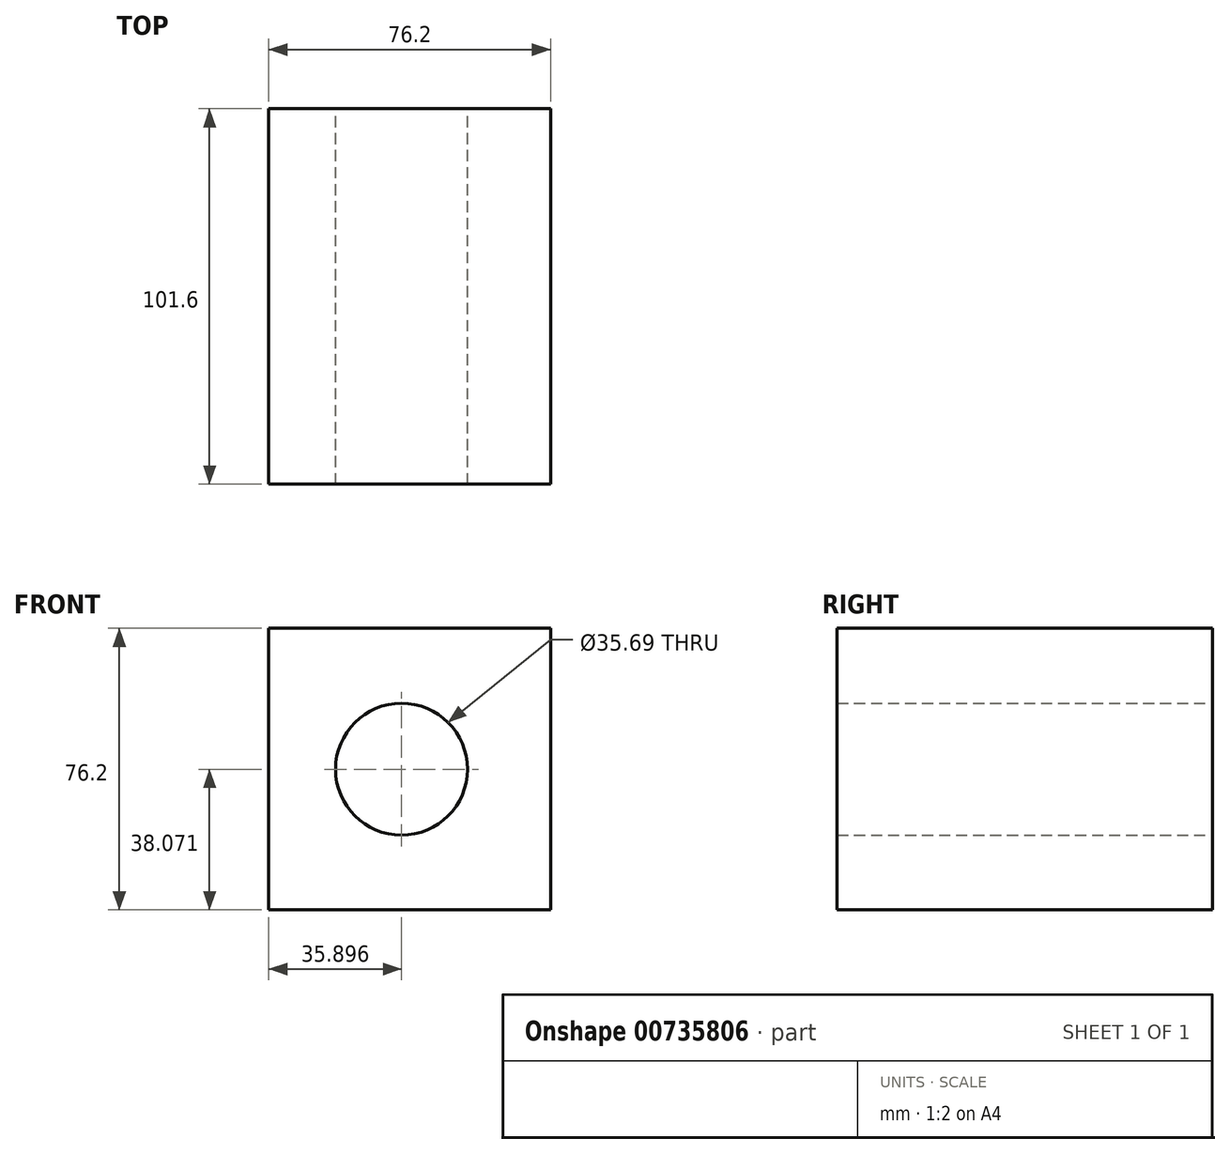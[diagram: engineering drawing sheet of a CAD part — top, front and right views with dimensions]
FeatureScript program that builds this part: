
annotation { "Feature Type Name" : "Feature", "Feature Type Description" : "" }
export const myFeature = defineFeature(function(context is Context, id is Id, definition is map)
    precondition{}
    {
        {
            var Q0;
            Q0=qCreatedBy(makeId("Front.planeOp"),FACE);
            var sketch = newSketch(context, id + "F0", { "sketchPlane" : qUnion([Q0])});
            skLineSegment(sketch, "E0", {"start": v(0, 0) * mm, "end": v(76.2, 0) * mm});
            skLineSegment(sketch, "E1", {"start": v(76.2, 0) * mm, "end": v(76.2, 76.2) * mm});
            skLineSegment(sketch, "E2", {"start": v(76.2, 76.2) * mm, "end": v(0, 76.2) * mm});
            skLineSegment(sketch, "E3", {"start": v(0, 76.2) * mm, "end": v(0, 0) * mm});
            skCircle(sketch, "E4", {"center": v(35.9, 38.07) * mm, "radius": 17.84 * mm});
            skSolve(sketch);
        }
        {
            var Q0;
            Q0=makeQuery(id+"F0.imprint","IMPRINT",FACE,{"disambiguationData":[TD([[makeQuery(id+"F0.imprint","IMPRINT",EDGE,{"derivedFrom":sQuery(id+"F0.wireOp",EDGE,"E0")}),1.0]])]});
            extrude(context, id + "F1", {"entities" : qUnion([Q0]), "depth" : 76.2 * mm, "offsetDistance" : 25.4 * mm});
        }
        {
            var Q0;
            Q0 = qSketchRegion(id + "F0", true);
            var Q1;
            Q1=makeQuery(id+"F1.opExtrude","CAP_FACE",FACE,{"disambiguationData":[OSD([sQuery(id+"F0.wireOp",EDGE,"E0"),sQuery(id+"F0.wireOp",EDGE,"E1"),sQuery(id+"F0.wireOp",EDGE,"E2"),sQuery(id+"F0.wireOp",EDGE,"E3"),sQuery(id+"F0.wireOp",EDGE,"E4")])],"isStart":false});
            extrude(context, id + "F2", {"entities" : qUnion([Q0, Q1]), "operationType" : NewBodyOperationType.ADD, "depth" : 25.4 * mm, "offsetDistance" : 25.4 * mm});
        }
    });
